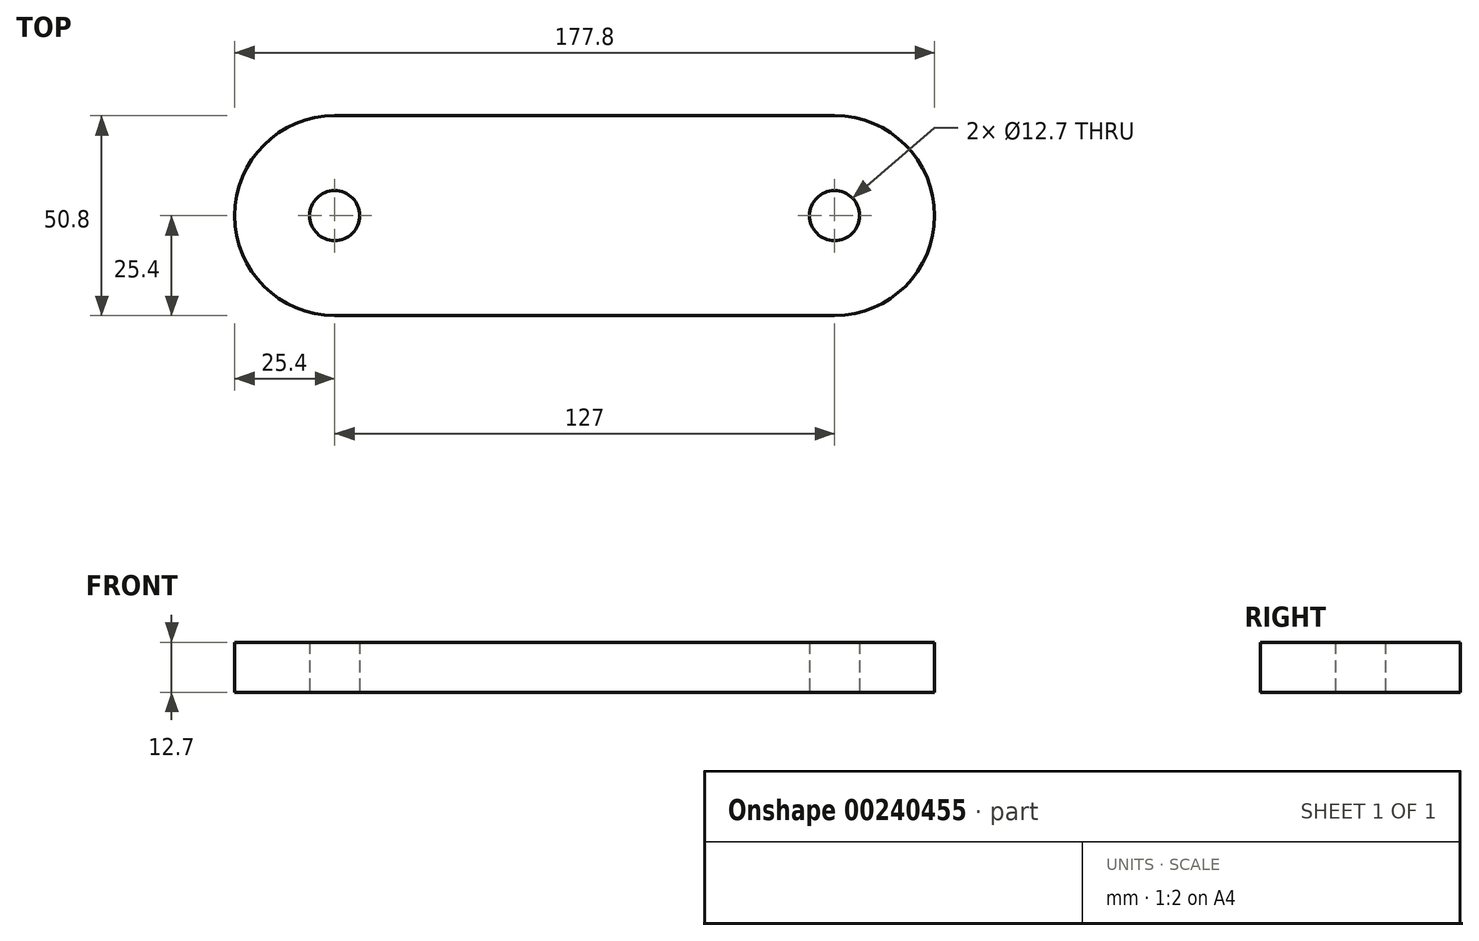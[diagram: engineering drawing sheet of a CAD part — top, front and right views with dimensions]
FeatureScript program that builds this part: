
annotation { "Feature Type Name" : "Feature", "Feature Type Description" : "" }
export const myFeature = defineFeature(function(context is Context, id is Id, definition is map)
    precondition{}
    {
        {
            var Q0;
            Q0=qCreatedBy(makeId("Top.planeOp"),FACE);
            var sketch = newSketch(context, id + "F0", { "sketchPlane" : qUnion([Q0])});
            skLineSegment(sketch, "E0.bottom", {"start": v(0, -25.4) * mm, "end": v(127, -25.4) * mm});
            skLineSegment(sketch, "E0.top", {"start": v(0, 25.4) * mm, "end": v(127, 25.4) * mm});
            skCircle(sketch, "E1", {"center": v(0, 0) * mm, "radius": 25.4 * mm});
            skCircle(sketch, "E2", {"center": v(127, 0) * mm, "radius": 25.4 * mm});
            skSolve(sketch);
        }
        {
            var Q0;
            {var subQ0=sQuery(id+"F0.wireOp",EDGE,"E1");var subQ1=makeQuery(id+"F0.imprint","INTERSECT",VERTEX,{"derivedFrom":[sQuery(id+"F0.wireOp",EDGE,"E0.bottom"),subQ0]});Q0=makeQuery(id+"F0.imprint","IMPRINT",FACE,{"disambiguationData":[TD([[makeQuery(id+"F0.imprint","IMPRINT",EDGE,{"disambiguationData":[TD([[subQ1,1.0]])],"derivedFrom":subQ0}),1.0]])]});}
            var sketch = newSketch(context, id + "F1", { "sketchPlane" : qUnion([Q0])});
            skCircle(sketch, "E3", {"center": v(0, 0) * mm, "radius": 6.35 * mm});
            skCircle(sketch, "E4", {"center": v(127.15, 0) * mm, "radius": 6.35 * mm});
            skSolve(sketch);
        }
        {
            var Q0;
            Q0 = qSketchRegion(id + "F0", true);
            extrude(context, id + "F2", {"entities" : qUnion([Q0]), "depth" : 12.7 * mm});
        }
        {
            var Q0;
            Q0=sQuery(id+"F1.wireOp",VERTEX,"E3.center");
            var Q1;
            Q1=makeQuery(id+"F2.opExtrude","SWEPT_BODY",BODY,{"disambiguationData":[OSD([sQuery(id+"F0.wireOp",EDGE,"E0.bottom"),sQuery(id+"F0.wireOp",EDGE,"E0.top"),sQuery(id+"F0.wireOp",EDGE,"E1"),sQuery(id+"F0.wireOp",EDGE,"E2")])]});
            hole(context, id + "F3", {"style" : HoleStyle.SIMPLE, "endStyle" : HoleEndStyle.BLIND, "oppositeDirection" : true, "holeDiameter" : 12.7 * mm, "holeDepth" : 25.4 * mm, "locations" : qUnion([Q0]), "scope" : qUnion([Q1])});
        }
        {
            var Q0;
            Q0=sQuery(id+"F0.wireOp",VERTEX,"E2.center");
            var Q1;
            Q1=makeQuery(id+"F2.opExtrude","SWEPT_BODY",BODY,{"disambiguationData":[OSD([sQuery(id+"F0.wireOp",EDGE,"E0.bottom"),sQuery(id+"F0.wireOp",EDGE,"E0.top"),sQuery(id+"F0.wireOp",EDGE,"E1"),sQuery(id+"F0.wireOp",EDGE,"E2")])]});
            hole(context, id + "F4", {"style" : HoleStyle.SIMPLE, "endStyle" : HoleEndStyle.BLIND, "oppositeDirection" : true, "holeDiameter" : 12.7 * mm, "holeDepth" : 127 * mm, "startFromSketch" : true, "locations" : qUnion([Q0]), "scope" : qUnion([Q1])});
        }
    });
